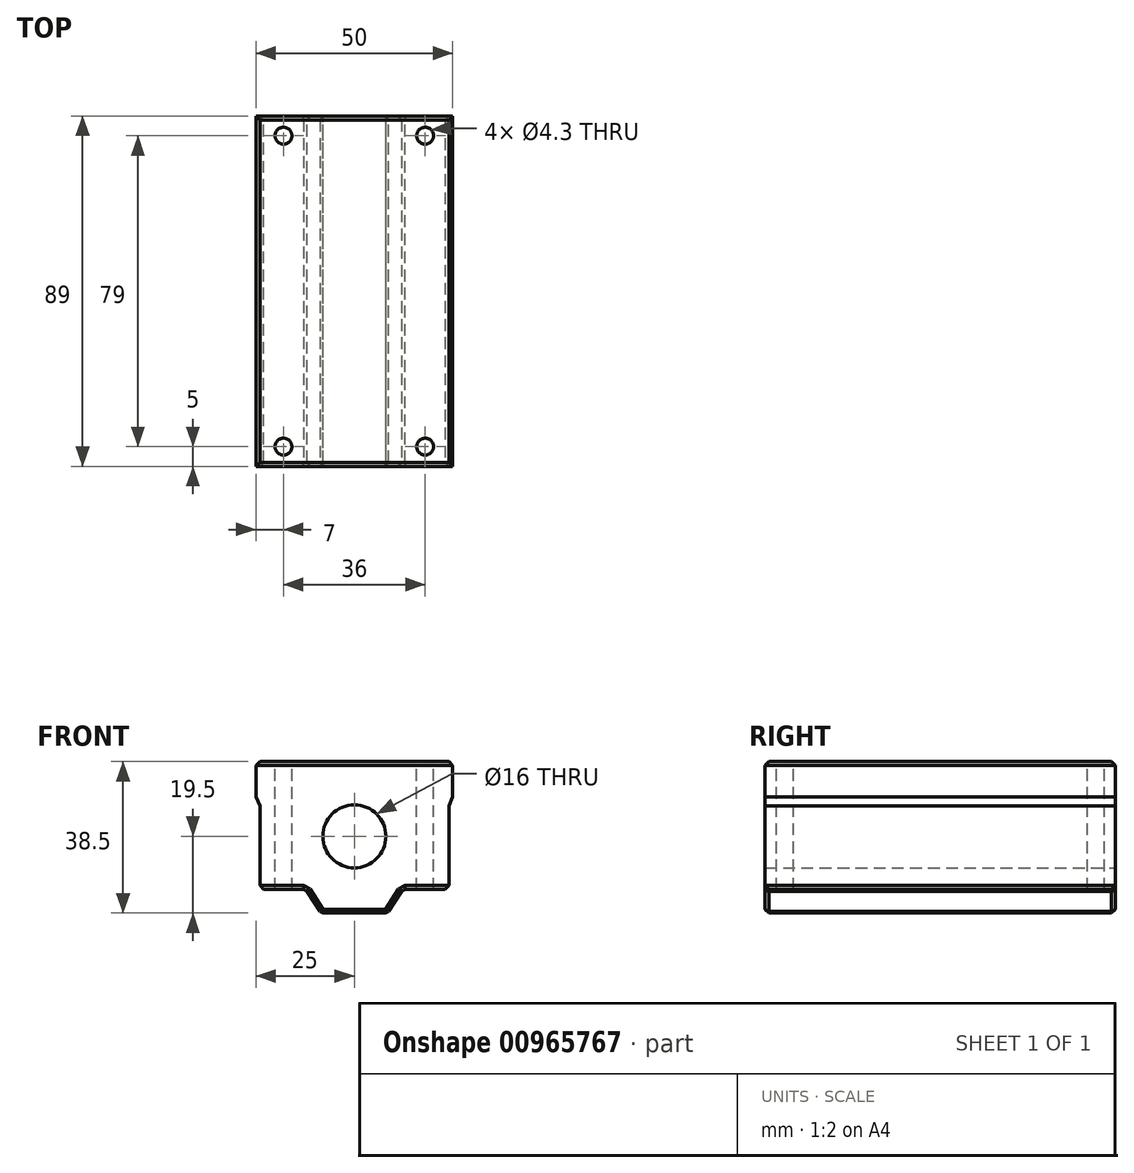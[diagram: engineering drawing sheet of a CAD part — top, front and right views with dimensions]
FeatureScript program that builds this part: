
annotation { "Feature Type Name" : "Feature", "Feature Type Description" : "" }
export const myFeature = defineFeature(function(context is Context, id is Id, definition is map)
    precondition{}
    {
        {
            var Q0;
            Q0=qCreatedBy(makeId("Front.planeOp"),FACE);
            var sketch = newSketch(context, id + "F0", { "sketchPlane" : qUnion([Q0])});
            skLineSegment(sketch, "E0", {"start": v(0, 19) * mm, "end": v(-25, 19) * mm});
            skLineSegment(sketch, "E1", {"start": v(-25, 19) * mm, "end": v(-25, 10) * mm});
            skLineSegment(sketch, "E2", {"start": v(-25, 10) * mm, "end": v(-24, 7.74) * mm});
            skLineSegment(sketch, "E3", {"start": v(-24, 7.74) * mm, "end": v(-24, -13.5) * mm});
            skLineSegment(sketch, "E4", {"start": v(-24, -13.5) * mm, "end": v(-12.35, -13.5) * mm});
            skLineSegment(sketch, "E5", {"start": v(-12.35, -13.5) * mm, "end": v(-8.43, -19.5) * mm});
            skLineSegment(sketch, "E6", {"start": v(-8.43, -19.5) * mm, "end": v(0, -19.5) * mm});
            skCircle(sketch, "E7", {"center": v(0, 0) * mm, "radius": 8 * mm});
            skLineSegment(sketch, "E8.MirrorCS", {"start": v(0, 19) * mm, "end": v(25, 19) * mm});
            skLineSegment(sketch, "E9.MirrorCS", {"start": v(25, 19) * mm, "end": v(25, 10) * mm});
            skLineSegment(sketch, "E10.MirrorCS", {"start": v(25, 10) * mm, "end": v(24, 7.74) * mm});
            skLineSegment(sketch, "E11.MirrorCS", {"start": v(24, 7.74) * mm, "end": v(24, -13.5) * mm});
            skLineSegment(sketch, "E12.MirrorCS", {"start": v(24, -13.5) * mm, "end": v(12.35, -13.5) * mm});
            skLineSegment(sketch, "E13.MirrorCS", {"start": v(12.35, -13.5) * mm, "end": v(8.43, -19.5) * mm});
            skLineSegment(sketch, "E14.MirrorCS", {"start": v(8.43, -19.5) * mm, "end": v(0, -19.5) * mm});
            skSolve(sketch);
        }
        {
            var Q0;
            Q0 = qSketchRegion(id + "F0", true);
            extrude(context, id + "F1", {"entities" : qUnion([Q0]), "endBound" : BoundingType.SYMMETRIC, "depth" : 89 * mm, "offsetDistance" : 25 * mm});
        }
        {
            var Q0;
            Q0=makeQuery(id+"F1.opExtrude","SWEPT_FACE",FACE,{"disambiguationData":[OSD([sQuery(id+"F0.wireOp",EDGE,"E0"),sQuery(id+"F0.wireOp",EDGE,"E8.MirrorCS")])]});
            var sketch = newSketch(context, id + "F2", { "sketchPlane" : qUnion([Q0])});
            skLineSegment(sketch, "E15.bottom", {"start": v(18, -39.5) * mm, "end": v(-18, -39.5) * mm, "construction": true});
            skLineSegment(sketch, "E15.top", {"start": v(18, 39.5) * mm, "end": v(-18, 39.5) * mm, "construction": true});
            skLineSegment(sketch, "E15.left", {"start": v(18, -39.5) * mm, "end": v(18, 39.5) * mm, "construction": true});
            skLineSegment(sketch, "E15.right", {"start": v(-18, -39.5) * mm, "end": v(-18, 39.5) * mm, "construction": true});
            skPoint(sketch, "E15.middle", {"position": v(0, 0) * mm});
            skSolve(sketch);
        }
        {
            var Q0;
            Q0=makeQuery(id+"F1.opExtrude","SWEPT_FACE",FACE,{"disambiguationData":[OSD([sQuery(id+"F0.wireOp",EDGE,"E0"),sQuery(id+"F0.wireOp",EDGE,"E8.MirrorCS")])]});
            var Q1;
            Q1=makeQuery(id+"F1.opExtrude","SWEPT_FACE",FACE,{"disambiguationData":[OSD([sQuery(id+"F0.wireOp",EDGE,"E6"),sQuery(id+"F0.wireOp",EDGE,"E14.MirrorCS")])]});
            var Q2;
            Q2=makeQuery(id+"F1.opExtrude","SWEPT_FACE",FACE,{"disambiguationData":[OSD([sQuery(id+"F0.wireOp",EDGE,"E12.MirrorCS")])]});
            var Q3;
            Q3=makeQuery(id+"F1.opExtrude","SWEPT_FACE",FACE,{"disambiguationData":[OSD([sQuery(id+"F0.wireOp",EDGE,"E4")])]});
            chamfer(context, id + "F3", {"entities" : qUnion([Q0, Q1, Q2, Q3]), "width" : 1 * mm, "tangentPropagation" : true});
        }
        {
            var Q0;
            Q0=sQuery(id+"F2.wireOp",VERTEX,"E15.top.end");
            var Q1;
            Q1=sQuery(id+"F2.wireOp",VERTEX,"E15.top.start");
            var Q2;
            Q2=sQuery(id+"F2.wireOp",VERTEX,"E15.bottom.start");
            var Q3;
            Q3=sQuery(id+"F2.wireOp",VERTEX,"E15.bottom.end");
            var Q4;
            Q4=makeQuery(id+"F1.opExtrude","SWEPT_BODY",BODY,{"disambiguationData":[OSD([sQuery(id+"F0.wireOp",EDGE,"E0"),sQuery(id+"F0.wireOp",EDGE,"E1"),sQuery(id+"F0.wireOp",EDGE,"E2"),sQuery(id+"F0.wireOp",EDGE,"E3"),sQuery(id+"F0.wireOp",EDGE,"E4"),sQuery(id+"F0.wireOp",EDGE,"E5"),sQuery(id+"F0.wireOp",EDGE,"E6"),sQuery(id+"F0.wireOp",EDGE,"E7"),sQuery(id+"F0.wireOp",EDGE,"E8.MirrorCS"),sQuery(id+"F0.wireOp",EDGE,"E9.MirrorCS"),sQuery(id+"F0.wireOp",EDGE,"E10.MirrorCS"),sQuery(id+"F0.wireOp",EDGE,"E11.MirrorCS"),sQuery(id+"F0.wireOp",EDGE,"E12.MirrorCS"),sQuery(id+"F0.wireOp",EDGE,"E13.MirrorCS"),sQuery(id+"F0.wireOp",EDGE,"E14.MirrorCS")])]});
            hole(context, id + "F4", {"style" : HoleStyle.SIMPLE, "endStyle" : HoleEndStyle.THROUGH, "holeDiameter" : 4.3 * mm, "majorDiameter" : 5 * mm, "tappedDepth" : 12 * mm, "tapClearance" : 3, "locations" : qUnion([Q0, Q1, Q2, Q3]), "scope" : qUnion([Q4])});
        }
    });
